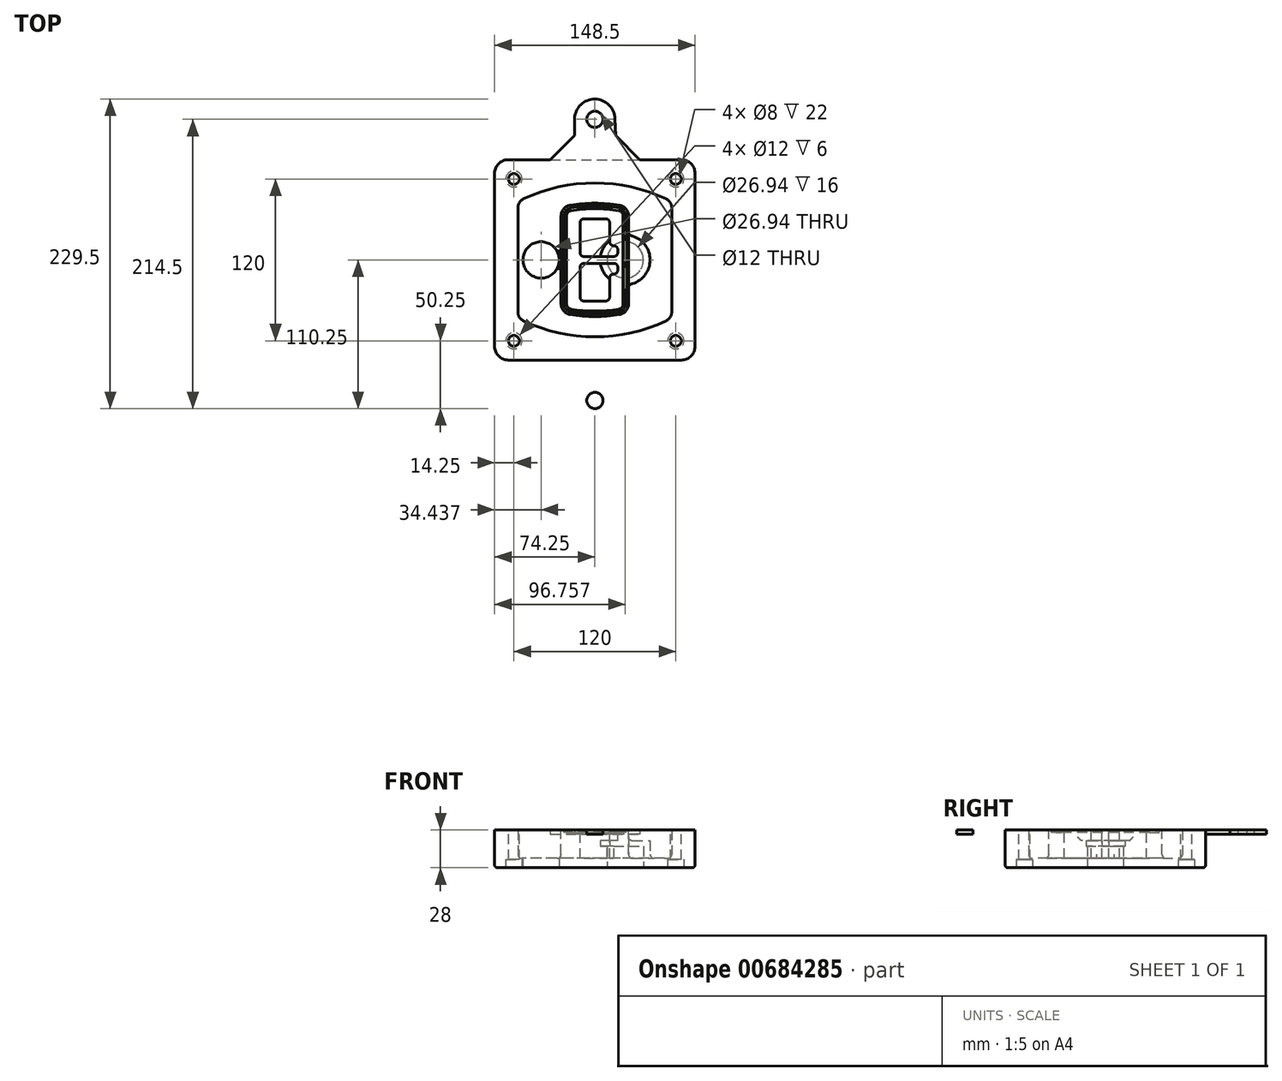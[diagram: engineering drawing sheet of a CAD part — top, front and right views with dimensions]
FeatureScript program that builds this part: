
annotation { "Feature Type Name" : "Feature", "Feature Type Description" : "" }
export const myFeature = defineFeature(function(context is Context, id is Id, definition is map)
    precondition{}
    {
        {
            var Q0;
            Q0=qCreatedBy(makeId("Top.planeOp"),FACE);
            var sketch = newSketch(context, id + "F0", { "sketchPlane" : qUnion([Q0])});
            skPoint(sketch, "E0.rect.middle", {"position": v(0, 0) * mm});
            skLineSegment(sketch, "E1.bottom", {"start": v(-64.25, -74.25) * mm, "end": v(64.25, -74.25) * mm});
            skLineSegment(sketch, "E1.top", {"start": v(-64.25, 74.25) * mm, "end": v(64.25, 74.25) * mm});
            skLineSegment(sketch, "E1.left", {"start": v(-74.25, -64.25) * mm, "end": v(-74.25, 64.25) * mm});
            skLineSegment(sketch, "E1.right", {"start": v(74.25, -64.25) * mm, "end": v(74.25, 64.25) * mm});
            skLineSegment(sketch, "E2", {"start": v(-74.25, 74.25) * mm, "end": v(74.25, -74.25) * mm, "construction": true});
            skLineSegment(sketch, "E3", {"start": v(74.25, 74.25) * mm, "end": v(-74.25, -74.25) * mm, "construction": true});
            skCircle(sketch, "E4", {"center": v(-60, 60) * mm, "radius": 4 * mm});
            skCircle(sketch, "E5", {"center": v(60, 60) * mm, "radius": 4 * mm});
            skCircle(sketch, "E6", {"center": v(60, -60) * mm, "radius": 4 * mm});
            skCircle(sketch, "E7", {"center": v(-60, -60) * mm, "radius": 4 * mm});
            skLineSegment(sketch, "E8", {"start": v(-60, 60) * mm, "end": v(60, 60) * mm, "construction": true});
            skLineSegment(sketch, "E9", {"start": v(60, 60) * mm, "end": v(60, -60) * mm, "construction": true});
            skLineSegment(sketch, "E10", {"start": v(60, -60) * mm, "end": v(-60, -60) * mm, "construction": true});
            skLineSegment(sketch, "E11", {"start": v(-60, -60) * mm, "end": v(-60, 60) * mm, "construction": true});
            skLineSegment(sketch, "E12", {"start": v(-60, 38.83) * mm, "end": v(-60, -38.83) * mm});
            skLineSegment(sketch, "E13", {"start": v(60, 38.83) * mm, "end": v(60, -38.83) * mm});
            skArc(sketch, "E14", {"start": v(54.26, 47.88) * mm, "mid": v(0, 60) * mm, "end": v(-54.26, 47.88) * mm});
            skArc(sketch, "E15", {"start": v(-54.26, -47.88) * mm, "mid": v(0, -60) * mm, "end": v(54.26, -47.88) * mm});
            skLineSegment(sketch, "E16", {"start": v(-60, 0) * mm, "end": v(60, 0) * mm, "construction": true});
            skPoint(sketch, "E17.visualSharp", {"position": v(-60, -45) * mm});
            skArc(sketch, "E17.filletArc", {"start": v(-60, -38.83) * mm, "mid": v(-58.44, -44.2) * mm, "end": v(-54.26, -47.88) * mm});
            skPoint(sketch, "E18.visualSharp", {"position": v(-60, 45) * mm});
            skArc(sketch, "E18.filletArc", {"start": v(-54.26, 47.88) * mm, "mid": v(-58.44, 44.2) * mm, "end": v(-60, 38.83) * mm});
            skPoint(sketch, "E19.visualSharp", {"position": v(60, 45) * mm});
            skArc(sketch, "E19.filletArc", {"start": v(60, 38.83) * mm, "mid": v(58.44, 44.2) * mm, "end": v(54.26, 47.88) * mm});
            skPoint(sketch, "E20.visualSharp", {"position": v(60, -45) * mm});
            skArc(sketch, "E20.filletArc", {"start": v(54.26, -47.88) * mm, "mid": v(58.44, -44.2) * mm, "end": v(60, -38.83) * mm});
            skPoint(sketch, "E21.visualSharp", {"position": v(-74.25, 74.25) * mm});
            skArc(sketch, "E21.filletArc", {"start": v(-64.25, 74.25) * mm, "mid": v(-71.32, 71.32) * mm, "end": v(-74.25, 64.25) * mm});
            skPoint(sketch, "E22.visualSharp", {"position": v(74.25, 74.25) * mm});
            skArc(sketch, "E22.filletArc", {"start": v(74.25, 64.25) * mm, "mid": v(71.32, 71.32) * mm, "end": v(64.25, 74.25) * mm});
            skPoint(sketch, "E23.visualSharp", {"position": v(74.25, -74.25) * mm});
            skArc(sketch, "E23.filletArc", {"start": v(64.25, -74.25) * mm, "mid": v(71.32, -71.32) * mm, "end": v(74.25, -64.25) * mm});
            skPoint(sketch, "E24.visualSharp", {"position": v(-74.25, -74.25) * mm});
            skArc(sketch, "E24.filletArc", {"start": v(-74.25, -64.25) * mm, "mid": v(-71.32, -71.32) * mm, "end": v(-64.25, -74.25) * mm});
            skArc(sketch, "E25.0", {"start": v(57, 38.83) * mm, "mid": v(55.9, 42.58) * mm, "end": v(52.98, 45.17) * mm});
            skLineSegment(sketch, "E25.1", {"start": v(57, 38.83) * mm, "end": v(57, -38.83) * mm});
            skArc(sketch, "E25.2", {"start": v(52.98, -45.17) * mm, "mid": v(55.9, -42.58) * mm, "end": v(57, -38.83) * mm});
            skArc(sketch, "E25.3", {"start": v(-52.98, -45.17) * mm, "mid": v(0, -57) * mm, "end": v(52.98, -45.17) * mm});
            skArc(sketch, "E25.4", {"start": v(-57, -38.83) * mm, "mid": v(-55.9, -42.58) * mm, "end": v(-52.98, -45.17) * mm});
            skArc(sketch, "E25.5", {"start": v(52.98, 45.17) * mm, "mid": v(0, 57) * mm, "end": v(-52.98, 45.17) * mm});
            skLineSegment(sketch, "E25.6", {"start": v(-57, 38.83) * mm, "end": v(-57, -38.83) * mm});
            skArc(sketch, "E25.7", {"start": v(-52.98, 45.17) * mm, "mid": v(-55.9, 42.58) * mm, "end": v(-57, 38.83) * mm});
            skArc(sketch, "E26.0", {"start": v(-55.96, 51.5) * mm, "mid": v(-61.82, 46.33) * mm, "end": v(-64, 38.83) * mm});
            skArc(sketch, "E26.1", {"start": v(55.96, 51.5) * mm, "mid": v(0, 64) * mm, "end": v(-55.96, 51.5) * mm});
            skArc(sketch, "E26.2", {"start": v(64, 38.83) * mm, "mid": v(61.82, 46.33) * mm, "end": v(55.96, 51.5) * mm});
            skLineSegment(sketch, "E26.3", {"start": v(64, 38.83) * mm, "end": v(64, -38.83) * mm});
            skArc(sketch, "E26.4", {"start": v(55.96, -51.5) * mm, "mid": v(61.82, -46.33) * mm, "end": v(64, -38.83) * mm});
            skLineSegment(sketch, "E26.5", {"start": v(-64, 38.83) * mm, "end": v(-64, -38.83) * mm});
            skArc(sketch, "E26.6", {"start": v(-55.96, -51.5) * mm, "mid": v(0, -64) * mm, "end": v(55.96, -51.5) * mm});
            skArc(sketch, "E26.7", {"start": v(-64, -38.83) * mm, "mid": v(-61.82, -46.33) * mm, "end": v(-55.96, -51.5) * mm});
            skSolve(sketch);
        }
        {
            var Q0;
            Q0=makeQuery(id+"F0.imprint","IMPRINT",FACE,{"disambiguationData":[TD([[makeQuery(id+"F0.imprint","IMPRINT",EDGE,{"derivedFrom":sQuery(id+"F0.wireOp",EDGE,"E1.bottom")}),1.0]])]});
            var Q1;
            Q1=makeQuery(id+"F0.imprint","IMPRINT",FACE,{"disambiguationData":[TD([[makeQuery(id+"F0.imprint","IMPRINT",EDGE,{"derivedFrom":sQuery(id+"F0.wireOp",EDGE,"E12")}),1.0]])]});
            var Q2;
            Q2=makeQuery(id+"F0.imprint","IMPRINT",FACE,{"disambiguationData":[TD([[makeQuery(id+"F0.imprint","IMPRINT",EDGE,{"derivedFrom":sQuery(id+"F0.wireOp",EDGE,"E25.0")}),1.0]])]});
            var Q3;
            Q3=makeQuery(id+"F0.imprint","IMPRINT",FACE,{"disambiguationData":[TD([[makeQuery(id+"F0.imprint","IMPRINT",EDGE,{"derivedFrom":sQuery(id+"F0.wireOp",EDGE,"E12")}),-1.0]])]});
            extrude(context, id + "F1", {"entities" : qUnion([Q0, Q1, Q2, Q3]), "oppositeDirection" : true, "depth" : 25 * mm});
        }
        {
            var Q0;
            Q0=makeQuery(id+"F0.imprint","IMPRINT",FACE,{"disambiguationData":[TD([[makeQuery(id+"F0.imprint","IMPRINT",EDGE,{"derivedFrom":sQuery(id+"F0.wireOp",EDGE,"E12")}),1.0]])]});
            extrude(context, id + "F2", {"entities" : qUnion([Q0]), "operationType" : NewBodyOperationType.ADD, "depth" : 3 * mm});
        }
        {
            var Q0;
            Q0=makeQuery(id+"F0.imprint","IMPRINT",FACE,{"disambiguationData":[TD([[makeQuery(id+"F0.imprint","IMPRINT",EDGE,{"derivedFrom":sQuery(id+"F0.wireOp",EDGE,"E25.0")}),1.0]])]});
            extrude(context, id + "F3", {"entities" : qUnion([Q0]), "operationType" : NewBodyOperationType.REMOVE, "oppositeDirection" : true, "depth" : 18 * mm});
        }
        {
            var Q0;
            Q0=makeQuery(id+"F2.opExtrude","CAP_FACE",FACE,{"disambiguationData":[OSD([sQuery(id+"F0.wireOp",EDGE,"E12"),sQuery(id+"F0.wireOp",EDGE,"E13"),sQuery(id+"F0.wireOp",EDGE,"E14"),sQuery(id+"F0.wireOp",EDGE,"E15"),sQuery(id+"F0.wireOp",EDGE,"E17.filletArc"),sQuery(id+"F0.wireOp",EDGE,"E18.filletArc"),sQuery(id+"F0.wireOp",EDGE,"E19.filletArc"),sQuery(id+"F0.wireOp",EDGE,"E20.filletArc"),sQuery(id+"F0.wireOp",EDGE,"E25.0"),sQuery(id+"F0.wireOp",EDGE,"E25.1"),sQuery(id+"F0.wireOp",EDGE,"E25.2"),sQuery(id+"F0.wireOp",EDGE,"E25.3"),sQuery(id+"F0.wireOp",EDGE,"E25.4"),sQuery(id+"F0.wireOp",EDGE,"E25.5"),sQuery(id+"F0.wireOp",EDGE,"E25.6"),sQuery(id+"F0.wireOp",EDGE,"E25.7")])],"isStart":false});
            var sketch = newSketch(context, id + "F4", { "sketchPlane" : qUnion([Q0])});
            skArc(sketch, "E27.0", {"start": v(-18.34, -40.45) * mm, "mid": v(0, -42) * mm, "end": v(18.34, -40.45) * mm});
            skArc(sketch, "E28.0", {"start": v(18.34, 40.45) * mm, "mid": v(0, 42) * mm, "end": v(-18.34, 40.45) * mm});
            skLineSegment(sketch, "E29", {"start": v(-25, 32.57) * mm, "end": v(-25, -32.57) * mm});
            skLineSegment(sketch, "E30", {"start": v(25, 32.57) * mm, "end": v(25, -32.57) * mm});
            skLineSegment(sketch, "E31", {"start": v(-25, 39.1) * mm, "end": v(25, 39.1) * mm, "construction": true});
            skLineSegment(sketch, "E32", {"start": v(-25, -39.1) * mm, "end": v(25, -39.1) * mm, "construction": true});
            skPoint(sketch, "E33.visualSharp", {"position": v(-25, 39.1) * mm});
            skArc(sketch, "E33.filletArc", {"start": v(-18.34, 40.45) * mm, "mid": v(-23.11, 37.73) * mm, "end": v(-25, 32.57) * mm});
            skPoint(sketch, "E34.visualSharp", {"position": v(25, 39.1) * mm});
            skArc(sketch, "E34.filletArc", {"start": v(25, 32.57) * mm, "mid": v(23.11, 37.73) * mm, "end": v(18.34, 40.45) * mm});
            skPoint(sketch, "E35.visualSharp", {"position": v(25, -39.1) * mm});
            skArc(sketch, "E35.filletArc", {"start": v(18.34, -40.45) * mm, "mid": v(23.11, -37.73) * mm, "end": v(25, -32.57) * mm});
            skPoint(sketch, "E36.visualSharp", {"position": v(-25, -39.1) * mm});
            skArc(sketch, "E36.filletArc", {"start": v(-25, -32.57) * mm, "mid": v(-23.11, -37.73) * mm, "end": v(-18.34, -40.45) * mm});
            skArc(sketch, "E37.0", {"start": v(52.98, 45.17) * mm, "mid": v(0, 57) * mm, "end": v(-52.98, 45.17) * mm});
            skArc(sketch, "E37.1", {"start": v(-52.98, 45.17) * mm, "mid": v(-55.9, 42.58) * mm, "end": v(-57, 38.83) * mm});
            skLineSegment(sketch, "E37.2", {"start": v(-57, 38.83) * mm, "end": v(-57, -38.83) * mm});
            skArc(sketch, "E37.3", {"start": v(-57, -38.83) * mm, "mid": v(-55.9, -42.58) * mm, "end": v(-52.98, -45.17) * mm});
            skArc(sketch, "E37.4", {"start": v(-52.98, -45.17) * mm, "mid": v(0, -57) * mm, "end": v(52.98, -45.17) * mm});
            skArc(sketch, "E37.5", {"start": v(52.98, -45.17) * mm, "mid": v(55.9, -42.58) * mm, "end": v(57, -38.83) * mm});
            skLineSegment(sketch, "E37.6", {"start": v(57, 38.83) * mm, "end": v(57, -38.83) * mm});
            skArc(sketch, "E37.7", {"start": v(57, 38.83) * mm, "mid": v(55.9, 42.58) * mm, "end": v(52.98, 45.17) * mm});
            skLineSegment(sketch, "E38.0", {"start": v(23, 32.57) * mm, "end": v(23, -32.57) * mm});
            skArc(sketch, "E38.1", {"start": v(18, -38.48) * mm, "mid": v(21.58, -36.44) * mm, "end": v(23, -32.57) * mm});
            skArc(sketch, "E38.2", {"start": v(-18, -38.48) * mm, "mid": v(0, -40) * mm, "end": v(18, -38.48) * mm});
            skArc(sketch, "E38.3", {"start": v(-23, -32.57) * mm, "mid": v(-21.58, -36.44) * mm, "end": v(-18, -38.48) * mm});
            skLineSegment(sketch, "E38.4", {"start": v(-23, 32.57) * mm, "end": v(-23, -32.57) * mm});
            skArc(sketch, "E38.5", {"start": v(23, 32.57) * mm, "mid": v(21.58, 36.44) * mm, "end": v(18, 38.48) * mm});
            skArc(sketch, "E38.6", {"start": v(-18, 38.48) * mm, "mid": v(-21.58, 36.44) * mm, "end": v(-23, 32.57) * mm});
            skArc(sketch, "E38.7", {"start": v(18, 38.48) * mm, "mid": v(0, 40) * mm, "end": v(-18, 38.48) * mm});
            skArc(sketch, "E39.0", {"start": v(21, 32.57) * mm, "mid": v(20.06, 35.15) * mm, "end": v(17.67, 36.5) * mm});
            skLineSegment(sketch, "E39.1", {"start": v(21, 32.57) * mm, "end": v(21, -32.57) * mm});
            skArc(sketch, "E39.2", {"start": v(17.67, -36.5) * mm, "mid": v(20.06, -35.15) * mm, "end": v(21, -32.57) * mm});
            skArc(sketch, "E39.3", {"start": v(-17.67, -36.5) * mm, "mid": v(0, -38) * mm, "end": v(17.67, -36.5) * mm});
            skArc(sketch, "E39.4", {"start": v(-21, -32.57) * mm, "mid": v(-20.06, -35.15) * mm, "end": v(-17.67, -36.5) * mm});
            skArc(sketch, "E39.5", {"start": v(17.67, 36.5) * mm, "mid": v(0, 38) * mm, "end": v(-17.67, 36.5) * mm});
            skLineSegment(sketch, "E39.6", {"start": v(-21, 32.57) * mm, "end": v(-21, -32.57) * mm});
            skArc(sketch, "E39.7", {"start": v(-17.67, 36.5) * mm, "mid": v(-20.06, 35.15) * mm, "end": v(-21, 32.57) * mm});
            skLineSegment(sketch, "E40", {"start": v(-25, 0) * mm, "end": v(25, 0) * mm, "construction": true});
            skLineSegment(sketch, "E41", {"start": v(-11, 5.5) * mm, "end": v(-11, 27.5) * mm});
            skLineSegment(sketch, "E42", {"start": v(-8, 30.5) * mm, "end": v(8, 30.5) * mm});
            skLineSegment(sketch, "E43", {"start": v(11, 27.5) * mm, "end": v(11, 13.5) * mm});
            skLineSegment(sketch, "E44", {"start": v(14, 10.5) * mm, "end": v(14, 10.5) * mm});
            skLineSegment(sketch, "E45", {"start": v(17, 7.5) * mm, "end": v(17, 5.5) * mm});
            skLineSegment(sketch, "E46", {"start": v(14, 2.5) * mm, "end": v(-8, 2.5) * mm});
            skPoint(sketch, "E47.visualSharp", {"position": v(-11, 30.5) * mm});
            skArc(sketch, "E47.filletArc", {"start": v(-8, 30.5) * mm, "mid": v(-10.12, 29.62) * mm, "end": v(-11, 27.5) * mm});
            skPoint(sketch, "E48.visualSharp", {"position": v(11, 30.5) * mm});
            skArc(sketch, "E48.filletArc", {"start": v(11, 27.5) * mm, "mid": v(10.12, 29.62) * mm, "end": v(8, 30.5) * mm});
            skPoint(sketch, "E49.visualSharp", {"position": v(11, 10.5) * mm});
            skArc(sketch, "E49.filletArc", {"start": v(11, 13.5) * mm, "mid": v(11.88, 11.38) * mm, "end": v(14, 10.5) * mm});
            skPoint(sketch, "E50.visualSharp", {"position": v(17, 10.5) * mm});
            skArc(sketch, "E50.filletArc", {"start": v(17, 7.5) * mm, "mid": v(16.12, 9.62) * mm, "end": v(14, 10.5) * mm});
            skPoint(sketch, "E51.visualSharp", {"position": v(17, 2.5) * mm});
            skArc(sketch, "E51.filletArc", {"start": v(14, 2.5) * mm, "mid": v(16.12, 3.38) * mm, "end": v(17, 5.5) * mm});
            skPoint(sketch, "E52.visualSharp", {"position": v(-11, 2.5) * mm});
            skArc(sketch, "E52.filletArc", {"start": v(-11, 5.5) * mm, "mid": v(-10.12, 3.38) * mm, "end": v(-8, 2.5) * mm});
            skLineSegment(sketch, "E53.0.MirrorCS", {"start": v(14, -2.5) * mm, "end": v(-8, -2.5) * mm});
            skArc(sketch, "E54.0.MirrorCS", {"start": v(-11, -5.5) * mm, "mid": v(-10.12, -3.38) * mm, "end": v(-8, -2.5) * mm});
            skLineSegment(sketch, "E55.0.MirrorCS", {"start": v(-11, -5.5) * mm, "end": v(-11, -27.5) * mm});
            skArc(sketch, "E56.0.MirrorCS", {"start": v(-8, -30.5) * mm, "mid": v(-10.12, -29.62) * mm, "end": v(-11, -27.5) * mm});
            skLineSegment(sketch, "E57.0.MirrorCS", {"start": v(-8, -30.5) * mm, "end": v(8, -30.5) * mm});
            skArc(sketch, "E58.0.MirrorCS", {"start": v(11, -27.5) * mm, "mid": v(10.12, -29.62) * mm, "end": v(8, -30.5) * mm});
            skLineSegment(sketch, "E59.0.MirrorCS", {"start": v(11, -27.5) * mm, "end": v(11, -13.5) * mm});
            skArc(sketch, "E60.0.MirrorCS", {"start": v(11, -13.5) * mm, "mid": v(11.88, -11.38) * mm, "end": v(14, -10.5) * mm});
            skArc(sketch, "E61.0.MirrorCS", {"start": v(17, -7.5) * mm, "mid": v(16.12, -9.62) * mm, "end": v(14, -10.5) * mm});
            skLineSegment(sketch, "E62.0.MirrorCS", {"start": v(17, -7.5) * mm, "end": v(17, -5.5) * mm});
            skArc(sketch, "E63.0.MirrorCS", {"start": v(14, -2.5) * mm, "mid": v(16.12, -3.38) * mm, "end": v(17, -5.5) * mm});
            skSolve(sketch);
        }
        {
            var Q0;
            Q0=makeQuery(id+"F4.imprint","IMPRINT",FACE,{"disambiguationData":[TD([[makeQuery(id+"F4.imprint","IMPRINT",EDGE,{"derivedFrom":sQuery(id+"F4.wireOp",EDGE,"E27.0")}),1.0]])]});
            var Q1;
            Q1=makeQuery(id+"F4.imprint","IMPRINT",FACE,{"disambiguationData":[TD([[makeQuery(id+"F4.imprint","IMPRINT",EDGE,{"derivedFrom":sQuery(id+"F4.wireOp",EDGE,"E38.0")}),-1.0]])]});
            var Q2;
            Q2=makeQuery(id+"F4.imprint","IMPRINT",FACE,{"disambiguationData":[TD([[makeQuery(id+"F4.imprint","IMPRINT",EDGE,{"derivedFrom":sQuery(id+"F4.wireOp",EDGE,"E39.0")}),1.0]])]});
            extrude(context, id + "F5", {"entities" : qUnion([Q0, Q1, Q2]), "operationType" : NewBodyOperationType.ADD, "endBound" : BoundingType.UP_TO_NEXT, "oppositeDirection" : true, "depth" : 25 * mm});
        }
        {
            var Q0;
            Q0=makeQuery(id+"F4.imprint","IMPRINT",FACE,{"disambiguationData":[TD([[makeQuery(id+"F4.imprint","IMPRINT",EDGE,{"derivedFrom":sQuery(id+"F4.wireOp",EDGE,"E38.0")}),-1.0]])]});
            extrude(context, id + "F6", {"entities" : qUnion([Q0]), "operationType" : NewBodyOperationType.REMOVE, "oppositeDirection" : true, "depth" : 2 * mm});
        }
        {
            var Q0;
            Q0=makeQuery(id+"F1.opExtrude","CAP_FACE",FACE,{"disambiguationData":[OSD([sQuery(id+"F0.wireOp",EDGE,"E1.bottom"),sQuery(id+"F0.wireOp",EDGE,"E1.top"),sQuery(id+"F0.wireOp",EDGE,"E1.left"),sQuery(id+"F0.wireOp",EDGE,"E1.right"),sQuery(id+"F0.wireOp",EDGE,"E4"),sQuery(id+"F0.wireOp",EDGE,"E5"),sQuery(id+"F0.wireOp",EDGE,"E6"),sQuery(id+"F0.wireOp",EDGE,"E7"),sQuery(id+"F0.wireOp",EDGE,"E21.filletArc"),sQuery(id+"F0.wireOp",EDGE,"E22.filletArc"),sQuery(id+"F0.wireOp",EDGE,"E23.filletArc"),sQuery(id+"F0.wireOp",EDGE,"E24.filletArc")])],"isStart":false});
            var sketch = newSketch(context, id + "F7", { "sketchPlane" : qUnion([Q0])});
            skCircle(sketch, "E64", {"center": v(22.5, 0) * mm, "radius": 13.47 * mm});
            skCircle(sketch, "E65", {"center": v(-39.81, 0) * mm, "radius": 13.47 * mm});
            skLineSegment(sketch, "E66", {"start": v(74.25, 0) * mm, "end": v(-74.25, 0) * mm});
            skCircle(sketch, "E67", {"center": v(22.5, 0) * mm, "radius": 18.47 * mm});
            skCircle(sketch, "E68", {"center": v(60, -60) * mm, "radius": 6 * mm});
            skCircle(sketch, "E69", {"center": v(-60, -60) * mm, "radius": 6 * mm});
            skCircle(sketch, "E70", {"center": v(-60, 60) * mm, "radius": 6 * mm});
            skCircle(sketch, "E71", {"center": v(60, 60) * mm, "radius": 6 * mm});
            skSolve(sketch);
        }
        {
            var Q0;
            {var subQ1=sQuery(id+"F7.wireOp",EDGE,"E66");var subQ4=sQuery(id+"F7.wireOp",EDGE,"E64");var subQ6=makeQuery(id+"F7.imprint","INTERSECT",VERTEX,{"disambiguationData":[OD(0.0)],"derivedFrom":[subQ4,subQ1]});Q0=makeQuery(id+"F7.imprint","IMPRINT",FACE,{"disambiguationData":[TD([[makeQuery(id+"F7.imprint","IMPRINT",EDGE,{"disambiguationData":[TD([[subQ6,-1.0]])],"derivedFrom":subQ4}),-1.0]])]});}
            var Q1;
            {var subQ0=sQuery(id+"F7.wireOp",EDGE,"E66");var subQ1=sQuery(id+"F7.wireOp",EDGE,"E64");var subQ3=makeQuery(id+"F7.imprint","INTERSECT",VERTEX,{"disambiguationData":[OD(0.0)],"derivedFrom":[subQ1,subQ0]});Q1=makeQuery(id+"F7.imprint","IMPRINT",FACE,{"disambiguationData":[TD([[makeQuery(id+"F7.imprint","IMPRINT",EDGE,{"disambiguationData":[TD([[subQ3,-1.0]])],"derivedFrom":subQ1}),1.0]])]});}
            var Q2;
            {var subQ0=sQuery(id+"F7.wireOp",EDGE,"E66");var subQ1=sQuery(id+"F7.wireOp",EDGE,"E64");var subQ3=makeQuery(id+"F7.imprint","INTERSECT",VERTEX,{"disambiguationData":[OD(0.0)],"derivedFrom":[subQ1,subQ0]});Q2=makeQuery(id+"F7.imprint","IMPRINT",FACE,{"disambiguationData":[TD([[makeQuery(id+"F7.imprint","IMPRINT",EDGE,{"disambiguationData":[TD([[subQ3,1.0]])],"derivedFrom":subQ1}),1.0]])]});}
            var Q3;
            {var subQ1=sQuery(id+"F7.wireOp",EDGE,"E66");var subQ4=sQuery(id+"F7.wireOp",EDGE,"E64");var subQ6=makeQuery(id+"F7.imprint","INTERSECT",VERTEX,{"disambiguationData":[OD(0.0)],"derivedFrom":[subQ4,subQ1]});Q3=makeQuery(id+"F7.imprint","IMPRINT",FACE,{"disambiguationData":[TD([[makeQuery(id+"F7.imprint","IMPRINT",EDGE,{"disambiguationData":[TD([[subQ6,1.0]])],"derivedFrom":subQ4}),-1.0]])]});}
            extrude(context, id + "F8", {"entities" : qUnion([Q0, Q1, Q2, Q3]), "operationType" : NewBodyOperationType.ADD, "oppositeDirection" : true, "depth" : 20 * mm});
        }
        {
            var Q0;
            {var subQ0=sQuery(id+"F7.wireOp",EDGE,"E66");var subQ1=sQuery(id+"F7.wireOp",EDGE,"E64");var subQ3=makeQuery(id+"F7.imprint","INTERSECT",VERTEX,{"disambiguationData":[OD(0.0)],"derivedFrom":[subQ1,subQ0]});Q0=makeQuery(id+"F7.imprint","IMPRINT",FACE,{"disambiguationData":[TD([[makeQuery(id+"F7.imprint","IMPRINT",EDGE,{"disambiguationData":[TD([[subQ3,-1.0]])],"derivedFrom":subQ1}),1.0]])]});}
            var Q1;
            {var subQ0=sQuery(id+"F7.wireOp",EDGE,"E66");var subQ1=sQuery(id+"F7.wireOp",EDGE,"E64");var subQ3=makeQuery(id+"F7.imprint","INTERSECT",VERTEX,{"disambiguationData":[OD(0.0)],"derivedFrom":[subQ1,subQ0]});Q1=makeQuery(id+"F7.imprint","IMPRINT",FACE,{"disambiguationData":[TD([[makeQuery(id+"F7.imprint","IMPRINT",EDGE,{"disambiguationData":[TD([[subQ3,1.0]])],"derivedFrom":subQ1}),1.0]])]});}
            extrude(context, id + "F9", {"entities" : qUnion([Q0, Q1]), "operationType" : NewBodyOperationType.REMOVE, "oppositeDirection" : true, "depth" : 16 * mm});
        }
        {
            var Q0;
            {var subQ0=sQuery(id+"F7.wireOp",EDGE,"E66");var subQ1=sQuery(id+"F7.wireOp",EDGE,"E65");var subQ3=makeQuery(id+"F7.imprint","INTERSECT",VERTEX,{"disambiguationData":[OD(0.0)],"derivedFrom":[subQ1,subQ0]});Q0=makeQuery(id+"F7.imprint","IMPRINT",FACE,{"disambiguationData":[TD([[makeQuery(id+"F7.imprint","IMPRINT",EDGE,{"disambiguationData":[TD([[subQ3,-1.0]])],"derivedFrom":subQ1}),1.0]])]});}
            var Q1;
            {var subQ0=sQuery(id+"F7.wireOp",EDGE,"E66");var subQ1=sQuery(id+"F7.wireOp",EDGE,"E65");var subQ3=makeQuery(id+"F7.imprint","INTERSECT",VERTEX,{"disambiguationData":[OD(0.0)],"derivedFrom":[subQ1,subQ0]});Q1=makeQuery(id+"F7.imprint","IMPRINT",FACE,{"disambiguationData":[TD([[makeQuery(id+"F7.imprint","IMPRINT",EDGE,{"disambiguationData":[TD([[subQ3,1.0]])],"derivedFrom":subQ1}),1.0]])]});}
            extrude(context, id + "F10", {"entities" : qUnion([Q0, Q1]), "operationType" : NewBodyOperationType.REMOVE, "oppositeDirection" : true, "depth" : 25 * mm});
        }
        {
            var Q0;
            Q0=makeQuery(id+"F7.imprint","IMPRINT",FACE,{"disambiguationData":[TD([[makeQuery(id+"F7.imprint","IMPRINT",EDGE,{"derivedFrom":sQuery(id+"F7.wireOp",EDGE,"E68")}),1.0]])]});
            var Q1;
            Q1=makeQuery(id+"F7.imprint","IMPRINT",FACE,{"disambiguationData":[TD([[makeQuery(id+"F7.imprint","IMPRINT",EDGE,{"derivedFrom":makeQuery(id+"F1.opExtrude","CAP_EDGE",EDGE,{"disambiguationData":[OSD([sQuery(id+"F0.wireOp",EDGE,"E5")])],"isStart":false})}),-1.0]])]});
            var Q2;
            Q2=makeQuery(id+"F7.imprint","IMPRINT",FACE,{"disambiguationData":[TD([[makeQuery(id+"F7.imprint","IMPRINT",EDGE,{"derivedFrom":sQuery(id+"F7.wireOp",EDGE,"E69")}),1.0]])]});
            var Q3;
            Q3=makeQuery(id+"F7.imprint","IMPRINT",FACE,{"disambiguationData":[TD([[makeQuery(id+"F7.imprint","IMPRINT",EDGE,{"derivedFrom":makeQuery(id+"F1.opExtrude","CAP_EDGE",EDGE,{"disambiguationData":[OSD([sQuery(id+"F0.wireOp",EDGE,"E4")])],"isStart":false})}),-1.0]])]});
            var Q4;
            Q4=makeQuery(id+"F7.imprint","IMPRINT",FACE,{"disambiguationData":[TD([[makeQuery(id+"F7.imprint","IMPRINT",EDGE,{"derivedFrom":sQuery(id+"F7.wireOp",EDGE,"E70")}),1.0]])]});
            var Q5;
            Q5=makeQuery(id+"F7.imprint","IMPRINT",FACE,{"disambiguationData":[TD([[makeQuery(id+"F7.imprint","IMPRINT",EDGE,{"derivedFrom":makeQuery(id+"F1.opExtrude","CAP_EDGE",EDGE,{"disambiguationData":[OSD([sQuery(id+"F0.wireOp",EDGE,"E7")])],"isStart":false})}),-1.0]])]});
            var Q6;
            Q6=makeQuery(id+"F7.imprint","IMPRINT",FACE,{"disambiguationData":[TD([[makeQuery(id+"F7.imprint","IMPRINT",EDGE,{"derivedFrom":sQuery(id+"F7.wireOp",EDGE,"E71")}),1.0]])]});
            var Q7;
            Q7=makeQuery(id+"F7.imprint","IMPRINT",FACE,{"disambiguationData":[TD([[makeQuery(id+"F7.imprint","IMPRINT",EDGE,{"derivedFrom":makeQuery(id+"F1.opExtrude","CAP_EDGE",EDGE,{"disambiguationData":[OSD([sQuery(id+"F0.wireOp",EDGE,"E6")])],"isStart":false})}),-1.0]])]});
            extrude(context, id + "F11", {"entities" : qUnion([Q0, Q1, Q2, Q3, Q4, Q5, Q6, Q7]), "operationType" : NewBodyOperationType.REMOVE, "oppositeDirection" : true, "depth" : 6 * mm});
        }
        {
            var Q0;
            Q0=makeQuery(id+"F9.boolean.opBoolean","COPY",FACE,{"derivedFrom":makeQuery(id+"F9.opExtrude","CAP_FACE",FACE,{"disambiguationData":[OSD([sQuery(id+"F7.wireOp",EDGE,"E64")])],"isStart":false})});
            var sketch = newSketch(context, id + "F12", { "sketchPlane" : qUnion([Q0])});
            skArc(sketch, "E72.0", {"start": v(11, 14.45) * mm, "mid": v(6.45, 9.13) * mm, "end": v(4.2, 2.5) * mm});
            skArc(sketch, "E72.1", {"start": v(4.2, -2.5) * mm, "mid": v(6.45, -9.13) * mm, "end": v(11, -14.45) * mm});
            skLineSegment(sketch, "E73", {"start": v(4.2, -2.5) * mm, "end": v(14, -2.5) * mm});
            skLineSegment(sketch, "E74.0", {"start": v(14, 2.5) * mm, "end": v(4.2, 2.5) * mm});
            skArc(sketch, "E74.1", {"start": v(14, 2.5) * mm, "mid": v(16.12, 3.38) * mm, "end": v(17, 5.5) * mm});
            skLineSegment(sketch, "E74.2", {"start": v(17, 7.5) * mm, "end": v(17, 5.5) * mm});
            skArc(sketch, "E74.3", {"start": v(17, 7.5) * mm, "mid": v(16.12, 9.62) * mm, "end": v(14, 10.5) * mm});
            skArc(sketch, "E74.4", {"start": v(11, 13.5) * mm, "mid": v(11.88, 11.38) * mm, "end": v(14, 10.5) * mm});
            skLineSegment(sketch, "E74.5", {"start": v(11, 14.45) * mm, "end": v(11, 13.5) * mm});
            skLineSegment(sketch, "E74.7", {"start": v(14, -2.5) * mm, "end": v(4.2, -2.5) * mm});
            skArc(sketch, "E74.8", {"start": v(14, -2.5) * mm, "mid": v(16.12, -3.38) * mm, "end": v(17, -5.5) * mm});
            skLineSegment(sketch, "E74.9", {"start": v(17, -7.5) * mm, "end": v(17, -5.5) * mm});
            skArc(sketch, "E74.10", {"start": v(17, -7.5) * mm, "mid": v(16.12, -9.62) * mm, "end": v(14, -10.5) * mm});
            skArc(sketch, "E74.11", {"start": v(11, -13.5) * mm, "mid": v(11.88, -11.38) * mm, "end": v(14, -10.5) * mm});
            skLineSegment(sketch, "E74.12", {"start": v(11, -14.45) * mm, "end": v(11, -13.5) * mm});
            skPoint(sketch, "E75.orphan", {"position": v(11, -27.5) * mm});
            skPoint(sketch, "E76.orphan", {"position": v(-8, -2.5) * mm});
            skPoint(sketch, "E77.orphan", {"position": v(-8, 2.5) * mm});
            skPoint(sketch, "E78.orphan", {"position": v(11, 27.5) * mm});
            skSolve(sketch);
        }
        {
            var Q0;
            {var subQ7=sQuery(id+"F12.wireOp",EDGE,"E72.0");var subQ14=sQuery(id+"F12.wireOp",EDGE,"E72.1");var subQ16=sQuery(id+"F12.wireOp",EDGE,"E74.1");var subQ18=sQuery(id+"F12.wireOp",EDGE,"E74.8");Q0=qUnion([makeQuery(id+"F12.imprint","IMPRINT",FACE,{"disambiguationData":[TD([[makeQuery(id+"F12.imprint","IMPRINT",EDGE,{"derivedFrom":subQ7}),1.0]])]}),makeQuery(id+"F12.imprint","IMPRINT",FACE,{"disambiguationData":[TD([[makeQuery(id+"F12.imprint","IMPRINT",EDGE,{"derivedFrom":subQ14}),1.0]])]}),makeQuery(id+"F12.imprint","IMPRINT",FACE,{"disambiguationData":[TD([[makeQuery(id+"F12.imprint","IMPRINT",EDGE,{"derivedFrom":subQ16}),1.0]])]}),makeQuery(id+"F12.imprint","IMPRINT",FACE,{"disambiguationData":[TD([[makeQuery(id+"F12.imprint","IMPRINT",EDGE,{"derivedFrom":subQ18}),-1.0]])]})]);}
            var Q1;
            Q1=makeQuery(id+"F5.boolean.opBoolean","SPLIT",FACE,{"disambiguationData":[TD([makeQuery(id+"F5.opExtrude","SWEPT_FACE",FACE,{"disambiguationData":[OSD([sQuery(id+"F4.wireOp",EDGE,"E41")])]})])],"derivedFrom":makeQuery(id+"F3.boolean.opBoolean","COPY",FACE,{"derivedFrom":makeQuery(id+"F3.opExtrude","CAP_FACE",FACE,{"disambiguationData":[OSD([sQuery(id+"F0.wireOp",EDGE,"E25.0"),sQuery(id+"F0.wireOp",EDGE,"E25.1"),sQuery(id+"F0.wireOp",EDGE,"E25.2"),sQuery(id+"F0.wireOp",EDGE,"E25.3"),sQuery(id+"F0.wireOp",EDGE,"E25.4"),sQuery(id+"F0.wireOp",EDGE,"E25.5"),sQuery(id+"F0.wireOp",EDGE,"E25.6"),sQuery(id+"F0.wireOp",EDGE,"E25.7")])],"isStart":false})})});
            extrude(context, id + "F13", {"entities" : qUnion([Q0]), "operationType" : NewBodyOperationType.REMOVE, "endBound" : BoundingType.UP_TO_SURFACE, "endBoundEntityFace" : qUnion([Q1]), "depth" : 25 * mm});
        }
        {
            var Q0;
            Q0=makeQuery(id+"F3.boolean.opBoolean","COPY",EDGE,{"derivedFrom":makeQuery(id+"F3.opExtrude","CAP_EDGE",EDGE,{"disambiguationData":[OSD([sQuery(id+"F0.wireOp",EDGE,"E25.6")])],"isStart":false})});
            var Q1;
            Q1=makeQuery(id+"F8.boolean.opBoolean","INTERSECT",EDGE,{"derivedFrom":[makeQuery(id+"F5.opExtrude","SWEPT_FACE",FACE,{"disambiguationData":[OSD([sQuery(id+"F4.wireOp",EDGE,"E30")])]}),makeQuery(id+"F8.opExtrude","CAP_FACE",FACE,{"disambiguationData":[OSD([sQuery(id+"F7.wireOp",EDGE,"E67")])],"isStart":false})]});
            var Q2;
            Q2=makeQuery(id+"F8.boolean.opBoolean","INTERSECT",EDGE,{"disambiguationData":[OD(1.0)],"derivedFrom":[makeQuery(id+"F5.opExtrude","SWEPT_FACE",FACE,{"disambiguationData":[OSD([sQuery(id+"F4.wireOp",EDGE,"E30")])]}),makeQuery(id+"F8.opExtrude","SWEPT_FACE",FACE,{"disambiguationData":[OSD([sQuery(id+"F7.wireOp",EDGE,"E67")])]})]});
            var Q3;
            {var subQ0=sQuery(id+"F4.wireOp",EDGE,"E30");Q3=makeQuery(id+"F8.boolean.opBoolean","SPLIT",EDGE,{"disambiguationData":[TD([makeQuery(id+"F5.opExtrude","SWEPT_FACE",FACE,{"disambiguationData":[OSD([sQuery(id+"F4.wireOp",EDGE,"E35.filletArc")])]})])],"derivedFrom":makeQuery(id+"F5.opExtrude","CAP_EDGE",EDGE,{"disambiguationData":[OSD([subQ0])],"isStart":false})});}
            var Q4;
            {var subQ0=sQuery(id+"F0.wireOp",EDGE,"E25.7");var subQ1=sQuery(id+"F0.wireOp",EDGE,"E25.1");var subQ2=sQuery(id+"F0.wireOp",EDGE,"E25.6");var subQ3=sQuery(id+"F0.wireOp",EDGE,"E25.5");var subQ4=sQuery(id+"F0.wireOp",EDGE,"E25.4");var subQ5=sQuery(id+"F0.wireOp",EDGE,"E25.0");var subQ6=sQuery(id+"F0.wireOp",EDGE,"E25.2");var subQ7=sQuery(id+"F0.wireOp",EDGE,"E25.3");Q4=makeQuery(id+"F8.boolean.opBoolean","INTERSECT",EDGE,{"derivedFrom":[makeQuery(id+"F5.boolean.opBoolean","SPLIT",FACE,{"disambiguationData":[TD([makeQuery(id+"F2.opExtrude","SWEPT_FACE",FACE,{"disambiguationData":[OSD([subQ5])]})])],"derivedFrom":makeQuery(id+"F3.boolean.opBoolean","COPY",FACE,{"derivedFrom":makeQuery(id+"F3.opExtrude","CAP_FACE",FACE,{"disambiguationData":[OSD([subQ5,subQ1,subQ6,subQ7,subQ4,subQ3,subQ2,subQ0])],"isStart":false})})}),makeQuery(id+"F8.opExtrude","SWEPT_FACE",FACE,{"disambiguationData":[OSD([sQuery(id+"F7.wireOp",EDGE,"E67")])]})]});}
            var Q5;
            Q5=makeQuery(id+"F8.boolean.opBoolean","INTERSECT",EDGE,{"disambiguationData":[OD(0.0)],"derivedFrom":[makeQuery(id+"F5.opExtrude","SWEPT_FACE",FACE,{"disambiguationData":[OSD([sQuery(id+"F4.wireOp",EDGE,"E30")])]}),makeQuery(id+"F8.opExtrude","SWEPT_FACE",FACE,{"disambiguationData":[OSD([sQuery(id+"F7.wireOp",EDGE,"E67")])]})]});
            fillet(context, id + "F14", {"entities" : qUnion([Q0, Q1, Q2, Q3, Q4, Q5]), "radius" : 3 * mm, "tangentPropagation" : true, "allowEdgeOverflow" : false});
        }
        {
            var Q0;
            Q0=makeQuery(id+"F1.opExtrude","CAP_EDGE",EDGE,{"disambiguationData":[OSD([sQuery(id+"F0.wireOp",EDGE,"E1.bottom")])],"isStart":false});
            fillet(context, id + "F15", {"entities" : qUnion([Q0]), "radius" : 2 * mm, "tangentPropagation" : true, "allowEdgeOverflow" : false});
        }
        {
            var Q0;
            {var subQ0=sQuery(id+"F0.wireOp",EDGE,"E21.filletArc");var subQ1=sQuery(id+"F0.wireOp",EDGE,"E7");var subQ2=sQuery(id+"F0.wireOp",EDGE,"E6");var subQ3=sQuery(id+"F0.wireOp",EDGE,"E5");var subQ4=sQuery(id+"F0.wireOp",EDGE,"E4");var subQ5=sQuery(id+"F0.wireOp",EDGE,"E22.filletArc");var subQ6=sQuery(id+"F0.wireOp",EDGE,"E1.bottom");var subQ7=sQuery(id+"F0.wireOp",EDGE,"E1.right");var subQ8=sQuery(id+"F0.wireOp",EDGE,"E1.top");var subQ9=sQuery(id+"F0.wireOp",EDGE,"E1.left");var subQ10=sQuery(id+"F0.wireOp",EDGE,"E23.filletArc");var subQ11=sQuery(id+"F0.wireOp",EDGE,"E24.filletArc");Q0=makeQuery(id+"F2.boolean.opBoolean","SPLIT",FACE,{"disambiguationData":[TD([makeQuery(id+"F1.opExtrude","SWEPT_FACE",FACE,{"disambiguationData":[OSD([subQ6])]})])],"derivedFrom":makeQuery(id+"F1.opExtrude","CAP_FACE",FACE,{"disambiguationData":[OSD([subQ6,subQ8,subQ9,subQ7,subQ4,subQ3,subQ2,subQ1,subQ0,subQ5,subQ10,subQ11])],"isStart":true})});}
            var sketch = newSketch(context, id + "F16", { "sketchPlane" : qUnion([Q0])});
            skLineSegment(sketch, "E79", {"start": v(-32.99, 74.25) * mm, "end": v(-14.99, 92.25) * mm});
            skLineSegment(sketch, "E80", {"start": v(33.34, 74.25) * mm, "end": v(15.34, 92.25) * mm});
            skLineSegment(sketch, "E81", {"start": v(15.34, 92.25) * mm, "end": v(15, 104.67) * mm});
            skLineSegment(sketch, "E82", {"start": v(-14.99, 92.25) * mm, "end": v(-14.99, 104.83) * mm});
            skCircle(sketch, "E83", {"center": v(0, 104.25) * mm, "radius": 6 * mm});
            skArc(sketch, "E84", {"start": v(15, 104.67) * mm, "mid": v(0.08, 119.25) * mm, "end": v(-14.99, 104.83) * mm});
            skLineSegment(sketch, "E85", {"start": v(-74.25, 0) * mm, "end": v(74.25, 0) * mm});
            skCircle(sketch, "E86.MirrorC", {"center": v(0, -104.25) * mm, "radius": 6 * mm});
            skLineSegment(sketch, "E87.MirrorCS", {"start": v(-14.99, -92.25) * mm, "end": v(-14.99, -104.83) * mm});
            skLineSegment(sketch, "E88.MirrorCS", {"start": v(15.34, -92.25) * mm, "end": v(15, -104.67) * mm});
            skArc(sketch, "E89.MirrorCS", {"start": v(15, -104.67) * mm, "mid": v(0.08, -119.25) * mm, "end": v(-14.99, -104.83) * mm});
            skLineSegment(sketch, "E90.MirrorCS", {"start": v(33.34, -74.25) * mm, "end": v(15.34, -92.25) * mm});
            skLineSegment(sketch, "E91.MirrorCS", {"start": v(-32.99, -74.25) * mm, "end": v(-14.99, -92.25) * mm});
            skSolve(sketch);
        }
        {
            var Q0;
            {var subQ1=sQuery(id+"F16.wireOp",EDGE,"E79");Q0=makeQuery(id+"F16.imprint","IMPRINT",FACE,{"disambiguationData":[TD([[makeQuery(id+"F16.imprint","IMPRINT",EDGE,{"derivedFrom":subQ1}),-1.0]])]});}
            var Q1;
            Q1=makeQuery(id+"F16.imprint","IMPRINT",FACE,{"disambiguationData":[TD([[makeQuery(id+"F16.imprint","IMPRINT",EDGE,{"derivedFrom":makeQuery(id+"F1.opExtrude","CAP_EDGE",EDGE,{"disambiguationData":[OSD([sQuery(id+"F0.wireOp",EDGE,"E4")])],"isStart":true})}),-1.0]])]});
            var Q2;
            Q2=makeQuery(id+"F16.imprint","IMPRINT",FACE,{"disambiguationData":[TD([[makeQuery(id+"F16.imprint","IMPRINT",EDGE,{"derivedFrom":makeQuery(id+"F1.opExtrude","CAP_EDGE",EDGE,{"disambiguationData":[OSD([sQuery(id+"F0.wireOp",EDGE,"E6")])],"isStart":true})}),-1.0]])]});
            var Q3;
            Q3=makeQuery(id+"F16.imprint","IMPRINT",FACE,{"disambiguationData":[TD([[makeQuery(id+"F16.imprint","IMPRINT",EDGE,{"derivedFrom":sQuery(id+"F16.wireOp",EDGE,"E86.MirrorC")}),1.0]])]});
            extrude(context, id + "F17", {"entities" : qUnion([Q0, Q1, Q2, Q3]), "operationType" : NewBodyOperationType.ADD, "depth" : 3 * mm, "offsetDistance" : 25 * mm});
        }
    });
